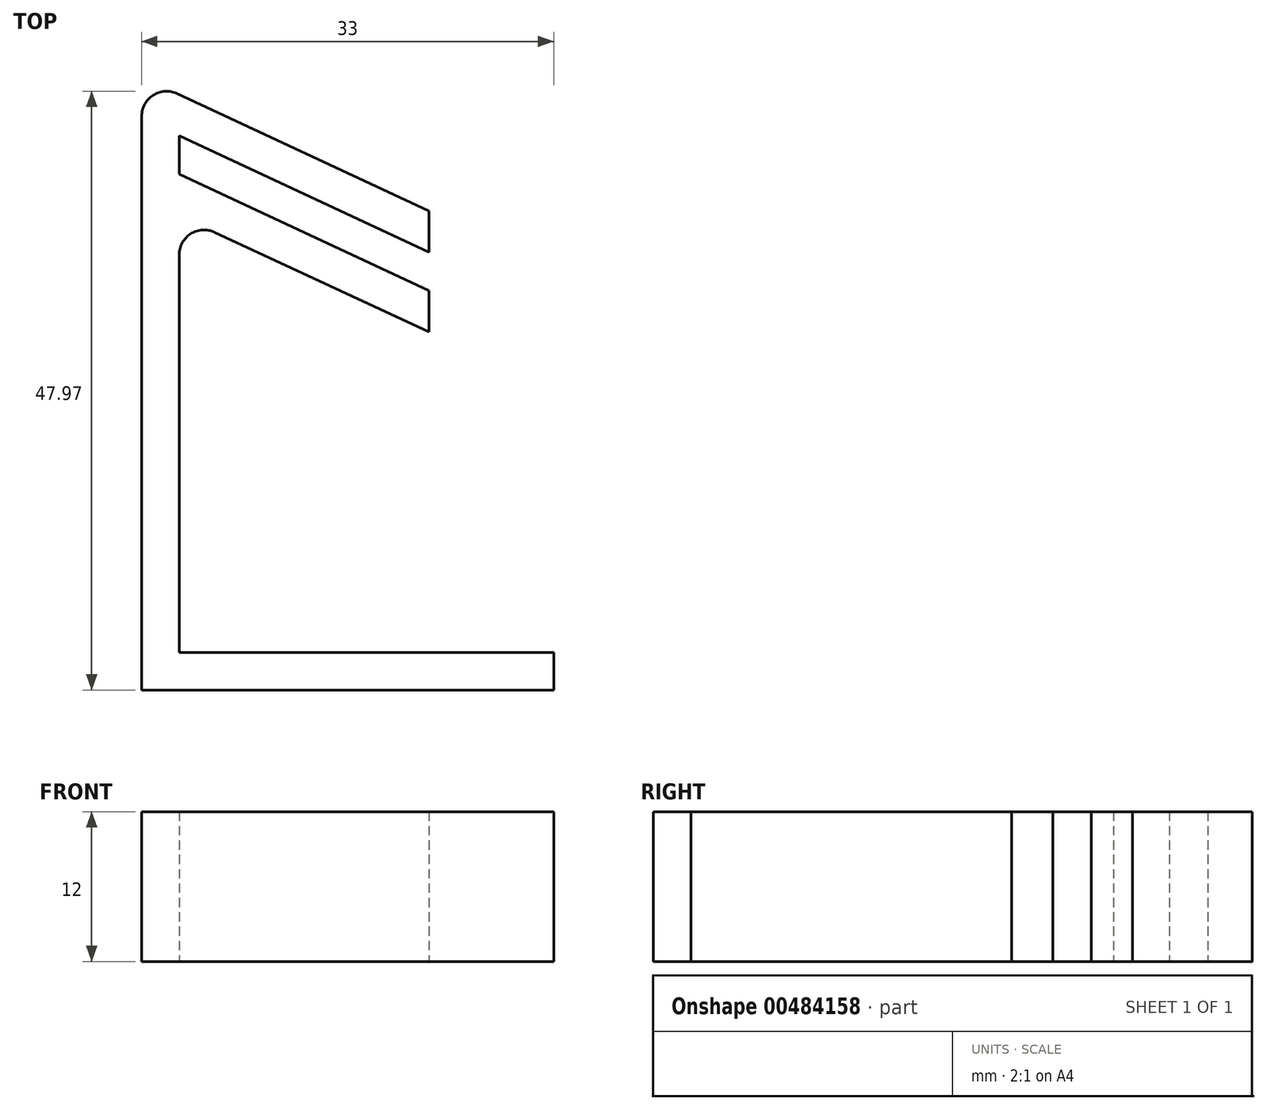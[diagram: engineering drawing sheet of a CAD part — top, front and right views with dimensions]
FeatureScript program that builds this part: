
annotation { "Feature Type Name" : "Feature", "Feature Type Description" : "" }
export const myFeature = defineFeature(function(context is Context, id is Id, definition is map)
    precondition{}
    {
        {
            var Q0;
            Q0=qCreatedBy(makeId("Top.planeOp"),FACE);
            var sketch = newSketch(context, id + "F0", { "sketchPlane" : qUnion([Q0])});
            skLineSegment(sketch, "E0", {"start": v(0, 0) * mm, "end": v(-20, 0) * mm});
            skLineSegment(sketch, "E1", {"start": v(-20, 0) * mm, "end": v(-20, 31.86) * mm});
            skLineSegment(sketch, "E2", {"start": v(-17.15, 33.67) * mm, "end": v(0, 25.67) * mm});
            skLineSegment(sketch, "E3", {"start": v(0, 25.67) * mm, "end": v(0, 0) * mm});
            skLineSegment(sketch, "E4.0", {"start": v(-23, 39.7) * mm, "end": v(1.27, 28.4) * mm});
            skLineSegment(sketch, "E4.1", {"start": v(-23, -3) * mm, "end": v(-23, 39.7) * mm});
            skLineSegment(sketch, "E4.2", {"start": v(0, -3) * mm, "end": v(-23, -3) * mm});
            skLineSegment(sketch, "E5", {"start": v(0, 25.67) * mm, "end": v(2.45, 30.93) * mm});
            skLineSegment(sketch, "E6", {"start": v(2.45, 30.93) * mm, "end": v(-20, 41.4) * mm});
            skLineSegment(sketch, "E7", {"start": v(-20, 41.4) * mm, "end": v(-18.73, 44.12) * mm, "construction": true});
            skLineSegment(sketch, "E8", {"start": v(-18.73, 44.12) * mm, "end": v(0, 35.38) * mm});
            skLineSegment(sketch, "E9", {"start": v(0, 35.38) * mm, "end": v(0, 25.67) * mm});
            skLineSegment(sketch, "E10", {"start": v(-18.73, 44.12) * mm, "end": v(-20.15, 44.78) * mm});
            skLineSegment(sketch, "E11", {"start": v(-23, 42.97) * mm, "end": v(-23, 39.7) * mm});
            skLineSegment(sketch, "E12", {"start": v(-20, 41.4) * mm, "end": v(-20, 38.31) * mm});
            skLineSegment(sketch, "E13", {"start": v(0, -3) * mm, "end": v(0, 0) * mm});
            skPoint(sketch, "E14.visualSharp", {"position": v(-23, 46.1) * mm});
            skArc(sketch, "E14.filletArc", {"start": v(-20.15, 44.78) * mm, "mid": v(-22.07, 44.66) * mm, "end": v(-23, 42.97) * mm});
            skPoint(sketch, "E15.visualSharp", {"position": v(-20, 35) * mm});
            skArc(sketch, "E15.filletArc", {"start": v(-17.15, 33.67) * mm, "mid": v(-19.07, 33.55) * mm, "end": v(-20, 31.86) * mm});
            skLineSegment(sketch, "E16", {"start": v(0, 0) * mm, "end": v(10, 0) * mm});
            skLineSegment(sketch, "E17", {"start": v(10, 0) * mm, "end": v(10, -3) * mm});
            skLineSegment(sketch, "E18", {"start": v(10, -3) * mm, "end": v(0, -3) * mm});
            skSolve(sketch);
        }
        {
            assignVariable(context, id + "F1", {"variableType" : VariableType.LENGTH, "name" : "Ancho", "lengthValue" : 12 * mm});
        }
        {
            var Q0;
            Q0=makeQuery(id+"F0.imprint","IMPRINT",FACE,{"disambiguationData":[TD([[makeQuery(id+"F0.imprint","IMPRINT",EDGE,{"derivedFrom":sQuery(id+"F0.wireOp",EDGE,"E13")}),-1.0]])]});
            var Q1;
            Q1=makeQuery(id+"F0.imprint","IMPRINT",FACE,{"disambiguationData":[TD([[makeQuery(id+"F0.imprint","IMPRINT",EDGE,{"derivedFrom":sQuery(id+"F0.wireOp",EDGE,"E0")}),1.0]])]});
            var Q2;
            {var subQ0=sQuery(id+"F0.wireOp",EDGE,"E8");Q2=makeQuery(id+"F0.imprint","IMPRINT",FACE,{"disambiguationData":[TD([[makeQuery(id+"F0.imprint","IMPRINT",EDGE,{"derivedFrom":subQ0}),-1.0]])]});}
            extrude(context, id + "F2", {"entities" : qUnion([Q0, Q1, Q2]), "offsetDistance" : 25 * mm, "depth" : getVariable(context, 'Ancho')});
        }
    });
